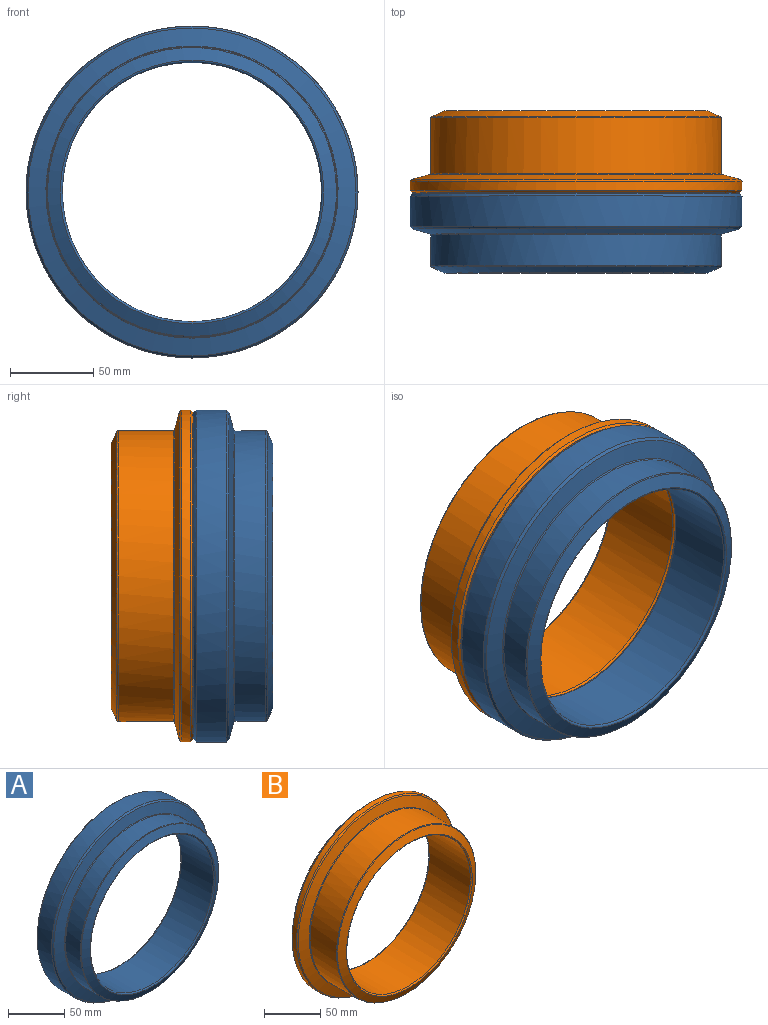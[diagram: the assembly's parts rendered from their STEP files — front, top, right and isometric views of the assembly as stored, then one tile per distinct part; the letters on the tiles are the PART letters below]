
ASSEMBLY  parts=2 mates=1
PART A: 20 faces, bbox 200x47.6x200 mm
  f0: plane 167.97x167.97mm, normal (0,1,0), area 2587mm2, adj f14,f19
  f1: cylinder r=85.26mm len=170.51mm, axis (0,-1,0), area 1768.8mm2, adj f17,f19
  f2: plane 184.02x184.02mm, normal (0,1,0), area 3558.1mm2, adj f17,f18
  f3: cylinder r=92.39mm len=184.79mm, axis (0,-1,0), area 2654.1mm2, adj f4,f18
  f4: cone r=92.39mm half-angle=45deg, axis (0,1,0), area 3846.4mm2, adj f3,f5
  f5: plane 195.57x195.57mm, normal (0,1,0), area 502.6mm2, adj f4,f11
  f6: cylinder r=99.44mm len=198.88mm, axis (0,-1,0), area 11244.6mm2, adj f11,f12
  f7: cone r=87mm half-angle=75deg, axis (0,1,0), area 6437.6mm2, adj f12,f15
  f8: cylinder r=87mm len=173.99mm, axis (0,-1,0), area 10132.6mm2, adj f15,f16
  f9: cone r=87mm half-angle=65deg, axis (0,1,0), area 4373.7mm2, adj f13,f16
  f10: cylinder r=77.66mm len=155.32mm, axis (0,-1,0), area 19768.5mm2, adj f13,f14
  f11: cone r=99.44mm half-angle=45deg, axis (0,-1,0), area 1450.3mm2, adj f5,f6
  f12: cone r=98.21mm half-angle=37.5deg, axis (0,1,0), area 1251.3mm2, adj f6,f7
  f13: torus R=78.93mm, axis (0,-1,0), area 979.2mm2, adj f9,f10
  f14: torus R=78.93mm, axis (0,1,0), area 979.2mm2, adj f0,f10
  f15: torus R=87.76mm, axis (0,-1,0), area 546.5mm2, adj f7,f8
  f16: torus R=86.23mm, axis (0,1,0), area 471.7mm2, adj f8,f9
  f17: torus R=85.64mm, axis (0,1,0), area 321.1mm2, adj f1,f2
  f18: torus R=92.01mm, axis (0,1,0), area 346.9mm2, adj f2,f3
  f19: torus R=83.99mm, axis (0,1,0), area 1062.8mm2, adj f0,f1
PART B: 14 faces, bbox 198.9x54x198.9 mm
  f0: cylinder r=87.19mm len=174.37mm, axis (0,-1,0), area 18183.5mm2, adj f8,f9
  f1: cone r=87.19mm half-angle=65.8deg, axis (0,1,0), area 4451.6mm2, adj f8,f12
  f2: cylinder r=77.66mm len=155.32mm, axis (0,-1,0), area 25098mm2, adj f12,f13
  f3: plane 184.53x184.53mm, normal (0,1,0), area 7171.9mm2, adj f4,f13
  f4: cone r=97.29mm half-angle=45deg, axis (0,-1,0), area 4235.6mm2, adj f3,f5
  f5: plane 196.34x196.34mm, normal (0,1,0), area 538.1mm2, adj f4,f11
  f6: cylinder r=99.44mm len=198.88mm, axis (0,-1,0), area 3401.7mm2, adj f10,f11
  f7: cone r=99.44mm half-angle=75deg, axis (0,1,0), area 6511.6mm2, adj f9,f10
  f8: torus R=86.42mm, axis (0,1,0), area 478.9mm2, adj f0,f1
  f9: torus R=87.95mm, axis (0,-1,0), area 547.7mm2, adj f0,f7
  f10: cone r=98.5mm half-angle=37.5deg, axis (0,1,0), area 961.5mm2, adj f6,f7
  f11: cone r=99.44mm half-angle=45deg, axis (0,-1,0), area 1115mm2, adj f5,f6
  f12: torus R=78.93mm, axis (0,1,0), area 979.2mm2, adj f1,f2
  f13: torus R=78.93mm, axis (0,-1,0), area 979.2mm2, adj f2,f3
PLACE A t=(-0.29,-3.73,-1.04)mm
PLACE B rot(axis=(1,0,0),180deg) t=(-0.29,44.79,-1.04)mm
MATE fastened A.f1 <-> B.f0  axis (0,-1,0) through (-0.29,-25.25,-1.04)mm
